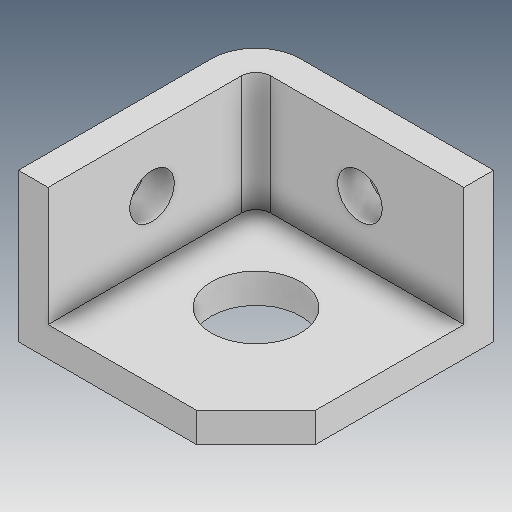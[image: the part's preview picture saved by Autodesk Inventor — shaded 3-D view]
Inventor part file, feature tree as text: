
AUTODESK INVENTOR PART (.ipt)
format: ipt  version: 2025 (Build 290162000, 162)  size: 164,352 bytes
history: native  units: mm
features: sketch x5, extrude x4, fillet x2
ambient origin geometry x8: Origin, YZ Plane, XZ Plane, XY Plane, X Axis, Y Axis, Z Axis, Center Point
bodies: 实体1 (feature_tree)
feature tree (11):
  sketch  "草图1"  dims[d4=80.0mm d5=80.0mm]
  extrude  "拉伸1"  Depth=80.0mm
  extrude  "拉伸2"  Depth=10.0mm
  fillet  "圆角1"  Radius=20.0mm
  fillet  "圆角2"  Radius=10.0mm
  extrude  "拉伸3"  Depth=10.0mm
  extrude  "拉伸4"  Depth=5.0mm
  sketch  "草图2"  dims[d6=30.0mm d7=20.0mm d8=20.0mm d9=10.0mm d10=0.0mm]
  sketch  "草图3"  dims[d11=10.0mm d12=10.0mm]
  sketch  "草图4"  dims[d13=40.0mm d14=0.0mm d15=5.0mm]
  sketch  "草图5"  dims[d16=15.0mm d17=15.0mm d18=20.0mm d19=35.0mm d20=40.0mm d21=0.0mm d22=15.0mm d23=35.0mm d24=20.0mm d25=10.0mm d26=0.0mm]
